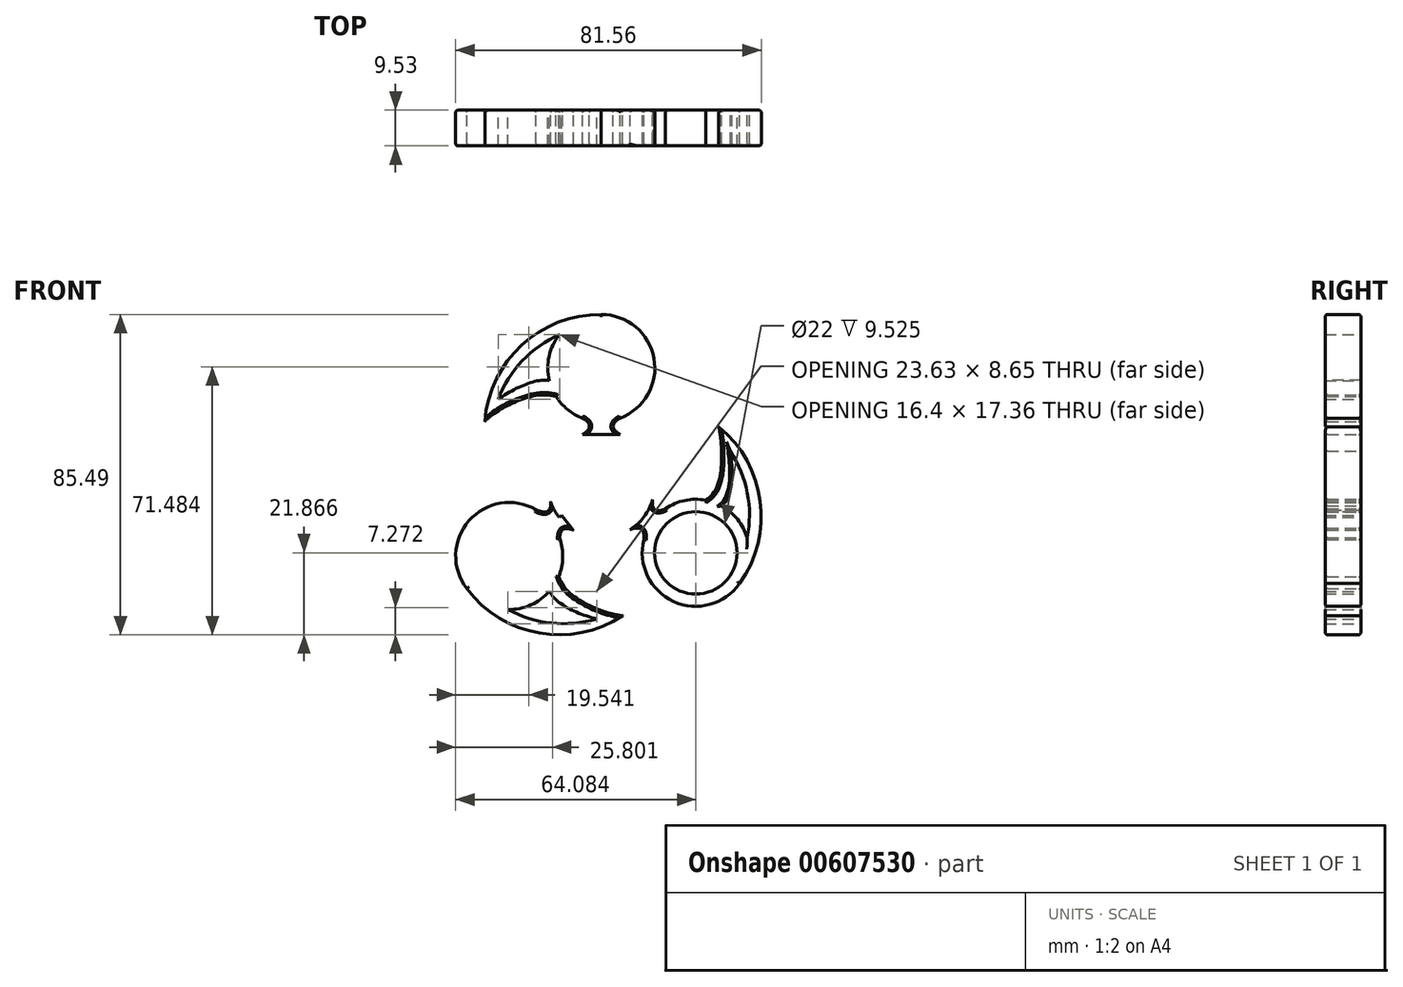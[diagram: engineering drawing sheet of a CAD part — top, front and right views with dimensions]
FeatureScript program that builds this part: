
annotation { "Feature Type Name" : "Feature", "Feature Type Description" : "" }
export const myFeature = defineFeature(function(context is Context, id is Id, definition is map)
    precondition{}
    {
        {
            var Q0;
            Q0=qCreatedBy(makeId("Front.planeOp"),FACE);
            var sketch = newSketch(context, id + "F0", { "sketchPlane" : qUnion([Q0])});
            skCircle(sketch, "E0", {"center": v(0, 0) * mm, "radius": 14.29 * mm});
            skLineSegment(sketch, "E1", {"start": v(0, 0) * mm, "end": v(0, 14.29) * mm});
            skLineSegment(sketch, "E2", {"start": v(0, 0) * mm, "end": v(-11.3, -8.76) * mm});
            skLineSegment(sketch, "E3", {"start": v(0, 0) * mm, "end": v(11.43, -8.57) * mm});
            skCircle(sketch, "E4", {"center": v(0, 31.12) * mm, "radius": 14.29 * mm});
            skLineSegment(sketch, "E5", {"start": v(0, 14.29) * mm, "end": v(0, 16.83) * mm});
            skArc(sketch, "E6", {"start": v(0, 45.4) * mm, "mid": v(-21.2, 37.27) * mm, "end": v(-31.1, 16.83) * mm});
            skFitSpline(sketch, "E7", {"points": [v(-31.1, 16.83) * mm, v(-17.35, 23.79) * mm, v(0, 16.83) * mm], "startDerivative": vector(18.3, 19.68) * mm, "endDerivative": vector(52.34, -33.11) * mm});
            skLineSegment(sketch, "E8", {"start": v(0, 15.56) * mm, "end": v(-3.18, 15.56) * mm});
            skPoint(sketch, "E8.endSnap0", {"position": v(0, 15.56) * mm});
            skLineSegment(sketch, "E9", {"start": v(0, 15.56) * mm, "end": v(3.18, 15.56) * mm});
            skLineSegment(sketch, "E10", {"start": v(0, 17.74) * mm, "end": v(5.03, 17.74) * mm});
            skLineSegment(sketch, "E11", {"start": v(0, 17.74) * mm, "end": v(-5.03, 17.74) * mm});
            skLineSegment(sketch, "E12", {"start": v(0, 14.29) * mm, "end": v(0, 13.37) * mm});
            skLineSegment(sketch, "E13", {"start": v(0, 13.37) * mm, "end": v(-5.03, 13.37) * mm});
            skLineSegment(sketch, "E14", {"start": v(0, 13.37) * mm, "end": v(5.03, 13.37) * mm});
            skFitSpline(sketch, "E15", {"points": [v(-5.03, 17.74) * mm, v(-3.18, 15.56) * mm, v(-5.03, 13.37) * mm], "startDerivative": vector(7.47, -4.37) * mm, "endDerivative": vector(-7.47, -4.37) * mm});
            skFitSpline(sketch, "E16", {"points": [v(5.03, 13.37) * mm, v(3.18, 15.56) * mm, v(5.03, 17.74) * mm], "startDerivative": vector(-7.47, 4.37) * mm, "endDerivative": vector(7.47, 4.37) * mm});
            skArc(sketch, "E17", {"start": v(4.36, 42.56) * mm, "mid": v(-16.61, 36.94) * mm, "end": v(-28.69, 18.9) * mm});
            skFitSpline(sketch, "E18", {"points": [v(-30.7, 19.98) * mm, v(-16.8, 27.72) * mm, v(0.44, 19.97) * mm], "startDerivative": vector(18.3, 19.68) * mm, "endDerivative": vector(52.34, -33.11) * mm});
            skLineSegment(sketch, "E19", {"start": v(-3.18, 15.56) * mm, "end": v(0, 14.29) * mm});
            skLineSegment(sketch, "E20", {"start": v(0, 14.29) * mm, "end": v(3.18, 15.56) * mm});
            skCircle(sketch, "E21", {"center": v(25.21, -18.22) * mm, "radius": 14.29 * mm});
            skLineSegment(sketch, "E22", {"start": v(11.43, -8.57) * mm, "end": v(13.51, -10.03) * mm});
            skArc(sketch, "E23", {"start": v(36.92, -26.42) * mm, "mid": v(42.42, -4.39) * mm, "end": v(31.34, 15.44) * mm});
            skFitSpline(sketch, "E24", {"points": [v(31.34, 15.44) * mm, v(30.71, -0.93) * mm, v(13.51, -10.03) * mm], "startDerivative": vector(5.62, -26.28) * mm, "endDerivative": vector(-57.15, -23.88) * mm});
            skLineSegment(sketch, "E25", {"start": v(12.47, -9.3) * mm, "end": v(14.3, -6.7) * mm});
            skPoint(sketch, "E25.endSnap0", {"position": v(12.47, -9.3) * mm});
            skLineSegment(sketch, "E26", {"start": v(12.47, -9.3) * mm, "end": v(10.65, -11.9) * mm});
            skLineSegment(sketch, "E27", {"start": v(14.26, -10.55) * mm, "end": v(11.38, -14.67) * mm});
            skLineSegment(sketch, "E28", {"start": v(14.26, -10.55) * mm, "end": v(17.14, -6.43) * mm});
            skArc(sketch, "E29", {"start": v(32.04, -28.23) * mm, "mid": v(39.54, -7.93) * mm, "end": v(31.84, 12.3) * mm});
            skFitSpline(sketch, "E30", {"points": [v(33.7, 13.3) * mm, v(33.83, -3.4) * mm, v(15.84, -12.2) * mm], "startDerivative": vector(5.62, -26.28) * mm, "endDerivative": vector(-57.15, -23.88) * mm});
            skLineSegment(sketch, "E31", {"start": v(14.3, -6.7) * mm, "end": v(11.8, -8.05) * mm});
            skLineSegment(sketch, "E32", {"start": v(11.43, -8.57) * mm, "end": v(10.65, -11.9) * mm});
            skLineSegment(sketch, "E33.0", {"start": v(14.3, -6.7) * mm, "end": v(12.47, -9.3) * mm, "construction": true});
            skCircle(sketch, "E34", {"center": v(-24.58, -19.07) * mm, "radius": 14.29 * mm});
            skLineSegment(sketch, "E35", {"start": v(-11.3, -8.76) * mm, "end": v(-13.26, -10.36) * mm});
            skArc(sketch, "E36", {"start": v(-35.91, -27.78) * mm, "mid": v(-16.54, -39.63) * mm, "end": v(5.7, -35.02) * mm});
            skFitSpline(sketch, "E37", {"points": [v(5.7, -35.02) * mm, v(-8.63, -28.76) * mm, v(-13.26, -10.36) * mm], "startDerivative": vector(-26.76, 2.52) * mm, "endDerivative": vector(-5.64, 61.68) * mm});
            skLineSegment(sketch, "E38", {"start": v(-12.27, -9.56) * mm, "end": v(-10.26, -12.02) * mm});
            skPoint(sketch, "E38.endSnap0", {"position": v(-12.27, -9.56) * mm});
            skLineSegment(sketch, "E39", {"start": v(-12.27, -9.56) * mm, "end": v(-14.28, -7.1) * mm});
            skLineSegment(sketch, "E40", {"start": v(-13.97, -10.94) * mm, "end": v(-17.43, -6.7) * mm});
            skLineSegment(sketch, "E41", {"start": v(-13.97, -10.94) * mm, "end": v(-11.04, -14.51) * mm});
            skArc(sketch, "E42", {"start": v(-36.27, -22.58) * mm, "mid": v(-19.07, -35.8) * mm, "end": v(2.57, -34.43) * mm});
            skFitSpline(sketch, "E43", {"points": [v(2.95, -36.62) * mm, v(-12.05, -30.77) * mm, v(-16.16, -11.65) * mm], "startDerivative": vector(-26.76, 2.52) * mm, "endDerivative": vector(-5.64, 61.68) * mm});
            skLineSegment(sketch, "E44", {"start": v(-10.26, -12.02) * mm, "end": v(-10.8, -9.23) * mm});
            skLineSegment(sketch, "E45", {"start": v(-11.3, -8.76) * mm, "end": v(-14.28, -7.1) * mm});
            skLineSegment(sketch, "E46.0", {"start": v(-10.26, -12.02) * mm, "end": v(-12.27, -9.56) * mm, "construction": true});
            skLineSegment(sketch, "E47", {"start": v(-11.3, -8.76) * mm, "end": v(-10.57, -8.2) * mm});
            skLineSegment(sketch, "E48", {"start": v(11.43, -8.57) * mm, "end": v(10.7, -8.02) * mm});
            skLineSegment(sketch, "E49", {"start": v(10.7, -8.02) * mm, "end": v(13.72, -4) * mm});
            skLineSegment(sketch, "E50", {"start": v(10.7, -8.02) * mm, "end": v(7.68, -12.05) * mm});
            skLineSegment(sketch, "E51", {"start": v(-10.57, -8.2) * mm, "end": v(-13.54, -4.56) * mm});
            skLineSegment(sketch, "E52", {"start": v(-10.57, -8.2) * mm, "end": v(-7.49, -12.17) * mm});
            skFitSpline(sketch, "E53", {"points": [v(-13.54, -4.56) * mm, v(-14.28, -7.1) * mm, v(-17.43, -6.7) * mm], "startDerivative": vector(0.73, -8.28) * mm, "endDerivative": vector(-8.38, 3.81) * mm});
            skFitSpline(sketch, "E54", {"points": [v(-11.04, -14.51) * mm, v(-10.26, -12.02) * mm, v(-7.49, -12.17) * mm], "startDerivative": vector(-0.57, 7.9) * mm, "endDerivative": vector(7.64, -3.14) * mm});
            skFitSpline(sketch, "E55", {"points": [v(7.68, -12.05) * mm, v(10.65, -11.9) * mm, v(11.38, -14.67) * mm], "startDerivative": vector(8.1, 3.32) * mm, "endDerivative": vector(-0.74, -8.6) * mm});
            skFitSpline(sketch, "E56", {"points": [v(13.72, -4) * mm, v(14.3, -6.7) * mm, v(17.14, -6.43) * mm], "startDerivative": vector(-1.06, -8.48) * mm, "endDerivative": vector(7.9, 3.59) * mm});
            skSolve(sketch);
        }
        {
            var Q0;
            {var subQ0=sQuery(id+"F0.wireOp",EDGE,"E6");var subQ1=sQuery(id+"F0.wireOp",EDGE,"E4");var subQ2=makeQuery(id+"F0.imprint","INTERSECT",VERTEX,{"derivedFrom":[subQ1,subQ0]});Q0=makeQuery(id+"F0.imprint","IMPRINT",FACE,{"disambiguationData":[TD([[makeQuery(id+"F0.imprint","IMPRINT",EDGE,{"disambiguationData":[TD([[subQ2,-1.0]])],"derivedFrom":subQ1}),-1.0]])]});}
            var Q1;
            {var subQ0=sQuery(id+"F0.wireOp",EDGE,"E18");var subQ1=sQuery(id+"F0.wireOp",EDGE,"E4");var subQ2=makeQuery(id+"F0.imprint","INTERSECT",VERTEX,{"derivedFrom":[subQ1,subQ0]});Q1=makeQuery(id+"F0.imprint","IMPRINT",FACE,{"disambiguationData":[TD([[makeQuery(id+"F0.imprint","IMPRINT",EDGE,{"disambiguationData":[TD([[subQ2,-1.0]])],"derivedFrom":subQ1}),-1.0]])]});}
            var Q2;
            {var subQ0=sQuery(id+"F0.wireOp",EDGE,"E7");var subQ1=sQuery(id+"F0.wireOp",EDGE,"E6");var subQ2=makeQuery(id+"F0.imprint","INTERSECT",VERTEX,{"derivedFrom":[subQ1,subQ0]});Q2=makeQuery(id+"F0.imprint","IMPRINT",FACE,{"disambiguationData":[TD([[makeQuery(id+"F0.imprint","IMPRINT",EDGE,{"disambiguationData":[TD([[subQ2,1.0]])],"derivedFrom":subQ1}),1.0]])]});}
            var Q3;
            {var subQ7=sQuery(id+"F0.wireOp",EDGE,"E10");Q3=makeQuery(id+"F0.imprint","IMPRINT",FACE,{"disambiguationData":[TD([[makeQuery(id+"F0.imprint","IMPRINT",EDGE,{"derivedFrom":subQ7}),1.0]])]});}
            var Q4;
            Q4=makeQuery(id+"F0.imprint","IMPRINT",FACE,{"disambiguationData":[TD([[makeQuery(id+"F0.imprint","IMPRINT",EDGE,{"derivedFrom":sQuery(id+"F0.wireOp",EDGE,"E1")}),1.0]])]});
            var Q5;
            Q5=makeQuery(id+"F0.imprint","IMPRINT",FACE,{"disambiguationData":[TD([[makeQuery(id+"F0.imprint","IMPRINT",EDGE,{"derivedFrom":sQuery(id+"F0.wireOp",EDGE,"E2")}),1.0]])]});
            var Q6;
            Q6=makeQuery(id+"F0.imprint","IMPRINT",FACE,{"disambiguationData":[TD([[makeQuery(id+"F0.imprint","IMPRINT",EDGE,{"derivedFrom":sQuery(id+"F0.wireOp",EDGE,"E1")}),-1.0]])]});
            var Q7;
            {var subQ7=sQuery(id+"F0.wireOp",EDGE,"E40");Q7=makeQuery(id+"F0.imprint","IMPRINT",FACE,{"disambiguationData":[TD([[makeQuery(id+"F0.imprint","IMPRINT",EDGE,{"derivedFrom":subQ7}),1.0]])]});}
            var Q8;
            {var subQ0=sQuery(id+"F0.wireOp",EDGE,"E36");var subQ1=sQuery(id+"F0.wireOp",EDGE,"E34");var subQ2=makeQuery(id+"F0.imprint","INTERSECT",VERTEX,{"derivedFrom":[subQ1,subQ0]});Q8=makeQuery(id+"F0.imprint","IMPRINT",FACE,{"disambiguationData":[TD([[makeQuery(id+"F0.imprint","IMPRINT",EDGE,{"disambiguationData":[TD([[subQ2,-1.0]])],"derivedFrom":subQ1}),-1.0]])]});}
            var Q9;
            {var subQ0=sQuery(id+"F0.wireOp",EDGE,"E43");var subQ1=sQuery(id+"F0.wireOp",EDGE,"E34");var subQ2=makeQuery(id+"F0.imprint","INTERSECT",VERTEX,{"derivedFrom":[subQ1,subQ0]});Q9=makeQuery(id+"F0.imprint","IMPRINT",FACE,{"disambiguationData":[TD([[makeQuery(id+"F0.imprint","IMPRINT",EDGE,{"disambiguationData":[TD([[subQ2,-1.0]])],"derivedFrom":subQ1}),-1.0]])]});}
            var Q10;
            {var subQ0=sQuery(id+"F0.wireOp",EDGE,"E37");var subQ1=sQuery(id+"F0.wireOp",EDGE,"E36");var subQ2=makeQuery(id+"F0.imprint","INTERSECT",VERTEX,{"derivedFrom":[subQ1,subQ0]});Q10=makeQuery(id+"F0.imprint","IMPRINT",FACE,{"disambiguationData":[TD([[makeQuery(id+"F0.imprint","IMPRINT",EDGE,{"disambiguationData":[TD([[subQ2,1.0]])],"derivedFrom":subQ1}),1.0]])]});}
            var Q11;
            {var subQ1=sQuery(id+"F0.wireOp",EDGE,"E34");var subQ3=sQuery(id+"F0.wireOp",EDGE,"E37");var subQ4=makeQuery(id+"F0.imprint","INTERSECT",VERTEX,{"derivedFrom":[subQ1,subQ3]});Q11=makeQuery(id+"F0.imprint","IMPRINT",FACE,{"disambiguationData":[TD([[makeQuery(id+"F0.imprint","IMPRINT",EDGE,{"disambiguationData":[TD([[subQ4,-1.0]])],"derivedFrom":subQ3}),-1.0]])]});}
            var Q12;
            {var subQ5=sQuery(id+"F0.wireOp",EDGE,"E27");Q12=makeQuery(id+"F0.imprint","IMPRINT",FACE,{"disambiguationData":[TD([[makeQuery(id+"F0.imprint","IMPRINT",EDGE,{"derivedFrom":subQ5}),1.0]])]});}
            var Q13;
            {var subQ0=sQuery(id+"F0.wireOp",EDGE,"E23");var subQ1=sQuery(id+"F0.wireOp",EDGE,"E21");var subQ2=makeQuery(id+"F0.imprint","INTERSECT",VERTEX,{"derivedFrom":[subQ1,subQ0]});Q13=makeQuery(id+"F0.imprint","IMPRINT",FACE,{"disambiguationData":[TD([[makeQuery(id+"F0.imprint","IMPRINT",EDGE,{"disambiguationData":[TD([[subQ2,-1.0]])],"derivedFrom":subQ1}),-1.0]])]});}
            var Q14;
            {var subQ0=sQuery(id+"F0.wireOp",EDGE,"E30");var subQ1=sQuery(id+"F0.wireOp",EDGE,"E21");var subQ2=makeQuery(id+"F0.imprint","INTERSECT",VERTEX,{"derivedFrom":[subQ1,subQ0]});Q14=makeQuery(id+"F0.imprint","IMPRINT",FACE,{"disambiguationData":[TD([[makeQuery(id+"F0.imprint","IMPRINT",EDGE,{"disambiguationData":[TD([[subQ2,-1.0]])],"derivedFrom":subQ1}),-1.0]])]});}
            var Q15;
            {var subQ0=sQuery(id+"F0.wireOp",EDGE,"E24");var subQ1=sQuery(id+"F0.wireOp",EDGE,"E23");var subQ2=makeQuery(id+"F0.imprint","INTERSECT",VERTEX,{"derivedFrom":[subQ1,subQ0]});Q15=makeQuery(id+"F0.imprint","IMPRINT",FACE,{"disambiguationData":[TD([[makeQuery(id+"F0.imprint","IMPRINT",EDGE,{"disambiguationData":[TD([[subQ2,1.0]])],"derivedFrom":subQ1}),1.0]])]});}
            var Q16;
            {var subQ0=sQuery(id+"F0.wireOp",EDGE,"E28");var subQ1=sQuery(id+"F0.wireOp",EDGE,"E21");var subQ2=makeQuery(id+"F0.imprint","INTERSECT",VERTEX,{"derivedFrom":[subQ1,subQ0]});Q16=makeQuery(id+"F0.imprint","IMPRINT",FACE,{"disambiguationData":[TD([[makeQuery(id+"F0.imprint","IMPRINT",EDGE,{"disambiguationData":[TD([[subQ2,1.0]])],"derivedFrom":subQ1}),1.0]])]});}
            var Q17;
            {var subQ3=sQuery(id+"F0.wireOp",EDGE,"E40");Q17=makeQuery(id+"F0.imprint","IMPRINT",FACE,{"disambiguationData":[TD([[makeQuery(id+"F0.imprint","IMPRINT",EDGE,{"derivedFrom":subQ3}),-1.0]])]});}
            var Q18;
            {var subQ0=sQuery(id+"F0.wireOp",EDGE,"E37");var subQ3=sQuery(id+"F0.wireOp",EDGE,"E41");var subQ5=makeQuery(id+"F0.imprint","INTERSECT",VERTEX,{"derivedFrom":[subQ0,subQ3]});Q18=makeQuery(id+"F0.imprint","IMPRINT",FACE,{"disambiguationData":[TD([[makeQuery(id+"F0.imprint","IMPRINT",EDGE,{"disambiguationData":[TD([[subQ5,-1.0]])],"derivedFrom":subQ0}),-1.0]])]});}
            var Q19;
            {var subQ0=sQuery(id+"F0.wireOp",EDGE,"E47");Q19=makeQuery(id+"F0.imprint","IMPRINT",FACE,{"disambiguationData":[TD([[makeQuery(id+"F0.imprint","IMPRINT",EDGE,{"derivedFrom":subQ0}),-1.0]])]});}
            var Q20;
            {var subQ0=sQuery(id+"F0.wireOp",EDGE,"E47");Q20=makeQuery(id+"F0.imprint","IMPRINT",FACE,{"disambiguationData":[TD([[makeQuery(id+"F0.imprint","IMPRINT",EDGE,{"derivedFrom":subQ0}),1.0]])]});}
            var Q21;
            {var subQ0=sQuery(id+"F0.wireOp",EDGE,"E45");Q21=makeQuery(id+"F0.imprint","IMPRINT",FACE,{"disambiguationData":[TD([[makeQuery(id+"F0.imprint","IMPRINT",EDGE,{"derivedFrom":subQ0}),-1.0]])]});}
            var Q22;
            {var subQ1=sQuery(id+"F0.wireOp",EDGE,"E0");var subQ3=sQuery(id+"F0.wireOp",EDGE,"E44");var subQ4=makeQuery(id+"F0.imprint","INTERSECT",VERTEX,{"derivedFrom":[subQ1,subQ3]});Q22=makeQuery(id+"F0.imprint","IMPRINT",FACE,{"disambiguationData":[TD([[makeQuery(id+"F0.imprint","IMPRINT",EDGE,{"disambiguationData":[TD([[subQ4,-1.0]])],"derivedFrom":subQ1}),-1.0]])]});}
            var Q23;
            {var subQ5=sQuery(id+"F0.wireOp",EDGE,"E38");Q23=makeQuery(id+"F0.imprint","IMPRINT",FACE,{"disambiguationData":[TD([[makeQuery(id+"F0.imprint","IMPRINT",EDGE,{"derivedFrom":subQ5}),-1.0]])]});}
            var Q24;
            {var subQ5=sQuery(id+"F0.wireOp",EDGE,"E39");Q24=makeQuery(id+"F0.imprint","IMPRINT",FACE,{"disambiguationData":[TD([[makeQuery(id+"F0.imprint","IMPRINT",EDGE,{"derivedFrom":subQ5}),1.0]])]});}
            var Q25;
            {var subQ2=sQuery(id+"F0.wireOp",EDGE,"E39");Q25=makeQuery(id+"F0.imprint","IMPRINT",FACE,{"disambiguationData":[TD([[makeQuery(id+"F0.imprint","IMPRINT",EDGE,{"derivedFrom":subQ2}),-1.0]])]});}
            var Q26;
            {var subQ5=sQuery(id+"F0.wireOp",EDGE,"E38");Q26=makeQuery(id+"F0.imprint","IMPRINT",FACE,{"disambiguationData":[TD([[makeQuery(id+"F0.imprint","IMPRINT",EDGE,{"derivedFrom":subQ5}),1.0]])]});}
            var Q27;
            {var subQ3=sQuery(id+"F0.wireOp",EDGE,"E27");Q27=makeQuery(id+"F0.imprint","IMPRINT",FACE,{"disambiguationData":[TD([[makeQuery(id+"F0.imprint","IMPRINT",EDGE,{"derivedFrom":subQ3}),-1.0]])]});}
            var Q28;
            {var subQ0=sQuery(id+"F0.wireOp",EDGE,"E24");var subQ3=sQuery(id+"F0.wireOp",EDGE,"E28");var subQ5=makeQuery(id+"F0.imprint","INTERSECT",VERTEX,{"derivedFrom":[subQ0,subQ3]});Q28=makeQuery(id+"F0.imprint","IMPRINT",FACE,{"disambiguationData":[TD([[makeQuery(id+"F0.imprint","IMPRINT",EDGE,{"disambiguationData":[TD([[subQ5,-1.0]])],"derivedFrom":subQ0}),-1.0]])]});}
            var Q29;
            {var subQ5=sQuery(id+"F0.wireOp",EDGE,"E25");Q29=makeQuery(id+"F0.imprint","IMPRINT",FACE,{"disambiguationData":[TD([[makeQuery(id+"F0.imprint","IMPRINT",EDGE,{"derivedFrom":subQ5}),-1.0]])]});}
            var Q30;
            {var subQ2=sQuery(id+"F0.wireOp",EDGE,"E25");Q30=makeQuery(id+"F0.imprint","IMPRINT",FACE,{"disambiguationData":[TD([[makeQuery(id+"F0.imprint","IMPRINT",EDGE,{"derivedFrom":subQ2}),1.0]])]});}
            var Q31;
            {var subQ0=sQuery(id+"F0.wireOp",EDGE,"E31");Q31=makeQuery(id+"F0.imprint","IMPRINT",FACE,{"disambiguationData":[TD([[makeQuery(id+"F0.imprint","IMPRINT",EDGE,{"derivedFrom":subQ0}),-1.0]])]});}
            var Q32;
            {var subQ0=sQuery(id+"F0.wireOp",EDGE,"E48");Q32=makeQuery(id+"F0.imprint","IMPRINT",FACE,{"disambiguationData":[TD([[makeQuery(id+"F0.imprint","IMPRINT",EDGE,{"derivedFrom":subQ0}),-1.0]])]});}
            var Q33;
            {var subQ0=sQuery(id+"F0.wireOp",EDGE,"E48");Q33=makeQuery(id+"F0.imprint","IMPRINT",FACE,{"disambiguationData":[TD([[makeQuery(id+"F0.imprint","IMPRINT",EDGE,{"derivedFrom":subQ0}),1.0]])]});}
            var Q34;
            {var subQ0=sQuery(id+"F0.wireOp",EDGE,"E32");Q34=makeQuery(id+"F0.imprint","IMPRINT",FACE,{"disambiguationData":[TD([[makeQuery(id+"F0.imprint","IMPRINT",EDGE,{"derivedFrom":subQ0}),-1.0]])]});}
            var Q35;
            {var subQ2=sQuery(id+"F0.wireOp",EDGE,"E26");Q35=makeQuery(id+"F0.imprint","IMPRINT",FACE,{"disambiguationData":[TD([[makeQuery(id+"F0.imprint","IMPRINT",EDGE,{"derivedFrom":subQ2}),-1.0]])]});}
            var Q36;
            {var subQ5=sQuery(id+"F0.wireOp",EDGE,"E26");Q36=makeQuery(id+"F0.imprint","IMPRINT",FACE,{"disambiguationData":[TD([[makeQuery(id+"F0.imprint","IMPRINT",EDGE,{"derivedFrom":subQ5}),1.0]])]});}
            var Q37;
            {var subQ1=sQuery(id+"F0.wireOp",EDGE,"E4");var subQ3=sQuery(id+"F0.wireOp",EDGE,"E7");var subQ4=makeQuery(id+"F0.imprint","INTERSECT",VERTEX,{"derivedFrom":[subQ1,subQ3]});Q37=makeQuery(id+"F0.imprint","IMPRINT",FACE,{"disambiguationData":[TD([[makeQuery(id+"F0.imprint","IMPRINT",EDGE,{"disambiguationData":[TD([[subQ4,-1.0]])],"derivedFrom":subQ3}),-1.0]])]});}
            var Q38;
            {var subQ0=sQuery(id+"F0.wireOp",EDGE,"E7");var subQ3=sQuery(id+"F0.wireOp",EDGE,"E11");var subQ5=makeQuery(id+"F0.imprint","INTERSECT",VERTEX,{"derivedFrom":[subQ0,subQ3]});Q38=makeQuery(id+"F0.imprint","IMPRINT",FACE,{"disambiguationData":[TD([[makeQuery(id+"F0.imprint","IMPRINT",EDGE,{"disambiguationData":[TD([[subQ5,-1.0]])],"derivedFrom":subQ0}),-1.0]])]});}
            var Q39;
            {var subQ5=sQuery(id+"F0.wireOp",EDGE,"E8");Q39=makeQuery(id+"F0.imprint","IMPRINT",FACE,{"disambiguationData":[TD([[makeQuery(id+"F0.imprint","IMPRINT",EDGE,{"derivedFrom":subQ5}),-1.0]])]});}
            var Q40;
            {var subQ0=sQuery(id+"F0.wireOp",EDGE,"E20");Q40=makeQuery(id+"F0.imprint","IMPRINT",FACE,{"disambiguationData":[TD([[makeQuery(id+"F0.imprint","IMPRINT",EDGE,{"derivedFrom":subQ0}),-1.0]])]});}
            var Q41;
            {var subQ0=sQuery(id+"F0.wireOp",EDGE,"E12");Q41=makeQuery(id+"F0.imprint","IMPRINT",FACE,{"disambiguationData":[TD([[makeQuery(id+"F0.imprint","IMPRINT",EDGE,{"derivedFrom":subQ0}),1.0]])]});}
            var Q42;
            {var subQ0=sQuery(id+"F0.wireOp",EDGE,"E12");Q42=makeQuery(id+"F0.imprint","IMPRINT",FACE,{"disambiguationData":[TD([[makeQuery(id+"F0.imprint","IMPRINT",EDGE,{"derivedFrom":subQ0}),-1.0]])]});}
            var Q43;
            {var subQ0=sQuery(id+"F0.wireOp",EDGE,"E19");Q43=makeQuery(id+"F0.imprint","IMPRINT",FACE,{"disambiguationData":[TD([[makeQuery(id+"F0.imprint","IMPRINT",EDGE,{"derivedFrom":subQ0}),-1.0]])]});}
            var Q44;
            {var subQ2=sQuery(id+"F0.wireOp",EDGE,"E8");Q44=makeQuery(id+"F0.imprint","IMPRINT",FACE,{"disambiguationData":[TD([[makeQuery(id+"F0.imprint","IMPRINT",EDGE,{"derivedFrom":subQ2}),1.0]])]});}
            var Q45;
            {var subQ2=sQuery(id+"F0.wireOp",EDGE,"E9");Q45=makeQuery(id+"F0.imprint","IMPRINT",FACE,{"disambiguationData":[TD([[makeQuery(id+"F0.imprint","IMPRINT",EDGE,{"derivedFrom":subQ2}),-1.0]])]});}
            var Q46;
            {var subQ5=sQuery(id+"F0.wireOp",EDGE,"E9");Q46=makeQuery(id+"F0.imprint","IMPRINT",FACE,{"disambiguationData":[TD([[makeQuery(id+"F0.imprint","IMPRINT",EDGE,{"derivedFrom":subQ5}),1.0]])]});}
            var Q47;
            {var subQ3=sQuery(id+"F0.wireOp",EDGE,"E10");Q47=makeQuery(id+"F0.imprint","IMPRINT",FACE,{"disambiguationData":[TD([[makeQuery(id+"F0.imprint","IMPRINT",EDGE,{"derivedFrom":subQ3}),-1.0]])]});}
            extrude(context, id + "F1", {"entities" : qUnion([Q0, Q1, Q2, Q3, Q4, Q5, Q6, Q7, Q8, Q9, Q10, Q11, Q12, Q13, Q14, Q15, Q16, Q17, Q18, Q19, Q20, Q21, Q22, Q23, Q24, Q25, Q26, Q27, Q28, Q29, Q30, Q31, Q32, Q33, Q34, Q35, Q36, Q37, Q38, Q39, Q40, Q41, Q42, Q43, Q44, Q45, Q46, Q47]), "depth" : 9.52 * mm, "offsetDistance" : 25.4 * mm});
        }
        {
            var Q0;
            {var subQ0=sQuery(id+"F0.wireOp",EDGE,"E4");Q0=makeQuery(id+"F1.opExtrude","CAP_EDGE",EDGE,{"disambiguationData":[OSD([subQ0]),TDD([makeQuery(id+"F0.imprint","IMPRINT",EDGE,{"disambiguationData":[TD([[makeQuery(id+"F0.imprint","INTERSECT",VERTEX,{"derivedFrom":[subQ0,sQuery(id+"F0.wireOp",EDGE,"E7")]}),-1.0]])],"derivedFrom":subQ0})])],"isStart":false});}
            var Q1;
            Q1=makeQuery(id+"F1.opExtrude","CAP_EDGE",EDGE,{"disambiguationData":[OSD([sQuery(id+"F0.wireOp",EDGE,"E15")])],"isStart":false});
            var Q2;
            {var subQ0=sQuery(id+"F0.wireOp",EDGE,"E0");Q2=makeQuery(id+"F1.opExtrude","CAP_EDGE",EDGE,{"disambiguationData":[OSD([subQ0]),TDD([makeQuery(id+"F0.imprint","IMPRINT",EDGE,{"disambiguationData":[TD([[makeQuery(id+"F0.imprint","INTERSECT",VERTEX,{"derivedFrom":[subQ0,sQuery(id+"F0.wireOp",EDGE,"E13"),sQuery(id+"F0.wireOp",EDGE,"E15")]}),-1.0]])],"derivedFrom":subQ0})])],"isStart":false});}
            var Q3;
            Q3=makeQuery(id+"F1.opExtrude","CAP_EDGE",EDGE,{"disambiguationData":[OSD([sQuery(id+"F0.wireOp",EDGE,"E53")])],"isStart":false});
            var Q4;
            {var subQ0=sQuery(id+"F0.wireOp",EDGE,"E34");Q4=makeQuery(id+"F1.opExtrude","CAP_EDGE",EDGE,{"disambiguationData":[OSD([subQ0]),TDD([makeQuery(id+"F0.imprint","IMPRINT",EDGE,{"disambiguationData":[TD([[makeQuery(id+"F0.imprint","INTERSECT",VERTEX,{"derivedFrom":[subQ0,sQuery(id+"F0.wireOp",EDGE,"E36")]}),1.0]])],"derivedFrom":subQ0})])],"isStart":false});}
            var Q5;
            Q5=makeQuery(id+"F1.opExtrude","CAP_EDGE",EDGE,{"disambiguationData":[OSD([sQuery(id+"F0.wireOp",EDGE,"E36")])],"isStart":false});
            var Q6;
            Q6=makeQuery(id+"F1.opExtrude","CAP_EDGE",EDGE,{"disambiguationData":[OSD([sQuery(id+"F0.wireOp",EDGE,"E37")])],"isStart":false});
            var Q7;
            Q7=makeQuery(id+"F1.opExtrude","CAP_FACE",FACE,{"disambiguationData":[OSD([sQuery(id+"F0.wireOp",EDGE,"E0"),sQuery(id+"F0.wireOp",EDGE,"E4"),sQuery(id+"F0.wireOp",EDGE,"E6"),sQuery(id+"F0.wireOp",EDGE,"E7"),sQuery(id+"F0.wireOp",EDGE,"E15"),sQuery(id+"F0.wireOp",EDGE,"E16"),sQuery(id+"F0.wireOp",EDGE,"E17"),sQuery(id+"F0.wireOp",EDGE,"E18"),sQuery(id+"F0.wireOp",EDGE,"E21"),sQuery(id+"F0.wireOp",EDGE,"E23"),sQuery(id+"F0.wireOp",EDGE,"E24"),sQuery(id+"F0.wireOp",EDGE,"E29"),sQuery(id+"F0.wireOp",EDGE,"E30"),sQuery(id+"F0.wireOp",EDGE,"E34"),sQuery(id+"F0.wireOp",EDGE,"E36"),sQuery(id+"F0.wireOp",EDGE,"E37"),sQuery(id+"F0.wireOp",EDGE,"E42"),sQuery(id+"F0.wireOp",EDGE,"E43"),sQuery(id+"F0.wireOp",EDGE,"E53"),sQuery(id+"F0.wireOp",EDGE,"E54"),sQuery(id+"F0.wireOp",EDGE,"E55"),sQuery(id+"F0.wireOp",EDGE,"E56")])],"isStart":false});
            var Q8;
            Q8=makeQuery(id+"F1.opExtrude","CAP_EDGE",EDGE,{"disambiguationData":[OSD([sQuery(id+"F0.wireOp",EDGE,"E7")])],"isStart":false});
            var Q9;
            Q9=makeQuery(id+"F1.opExtrude","CAP_EDGE",EDGE,{"disambiguationData":[OSD([sQuery(id+"F0.wireOp",EDGE,"E54")])],"isStart":false});
            var Q10;
            {var subQ0=sQuery(id+"F0.wireOp",EDGE,"E34");Q10=makeQuery(id+"F1.opExtrude","CAP_EDGE",EDGE,{"disambiguationData":[OSD([subQ0]),TDD([makeQuery(id+"F0.imprint","IMPRINT",EDGE,{"disambiguationData":[TD([[makeQuery(id+"F0.imprint","INTERSECT",VERTEX,{"derivedFrom":[subQ0,sQuery(id+"F0.wireOp",EDGE,"E37")]}),-1.0]])],"derivedFrom":subQ0})])],"isStart":false});}
            var Q11;
            {var subQ0=sQuery(id+"F0.wireOp",EDGE,"E0");Q11=makeQuery(id+"F1.opExtrude","CAP_EDGE",EDGE,{"disambiguationData":[OSD([subQ0]),TDD([makeQuery(id+"F0.imprint","IMPRINT",EDGE,{"disambiguationData":[TD([[makeQuery(id+"F0.imprint","INTERSECT",VERTEX,{"derivedFrom":[subQ0,sQuery(id+"F0.wireOp",EDGE,"E50"),sQuery(id+"F0.wireOp",EDGE,"E55")]}),1.0]])],"derivedFrom":subQ0})])],"isStart":false});}
            var Q12;
            Q12=makeQuery(id+"F1.opExtrude","CAP_EDGE",EDGE,{"disambiguationData":[OSD([sQuery(id+"F0.wireOp",EDGE,"E55")])],"isStart":false});
            var Q13;
            {var subQ0=sQuery(id+"F0.wireOp",EDGE,"E21");Q13=makeQuery(id+"F1.opExtrude","CAP_EDGE",EDGE,{"disambiguationData":[OSD([subQ0]),TDD([makeQuery(id+"F0.imprint","IMPRINT",EDGE,{"disambiguationData":[TD([[makeQuery(id+"F0.imprint","INTERSECT",VERTEX,{"derivedFrom":[subQ0,sQuery(id+"F0.wireOp",EDGE,"E23")]}),1.0]])],"derivedFrom":subQ0})])],"isStart":false});}
            var Q14;
            Q14=makeQuery(id+"F1.opExtrude","CAP_EDGE",EDGE,{"disambiguationData":[OSD([sQuery(id+"F0.wireOp",EDGE,"E23")])],"isStart":false});
            var Q15;
            Q15=makeQuery(id+"F1.opExtrude","CAP_EDGE",EDGE,{"disambiguationData":[OSD([sQuery(id+"F0.wireOp",EDGE,"E24")])],"isStart":false});
            var Q16;
            {var subQ0=sQuery(id+"F0.wireOp",EDGE,"E21");Q16=makeQuery(id+"F1.opExtrude","CAP_EDGE",EDGE,{"disambiguationData":[OSD([subQ0]),TDD([makeQuery(id+"F0.imprint","IMPRINT",EDGE,{"disambiguationData":[TD([[makeQuery(id+"F0.imprint","INTERSECT",VERTEX,{"derivedFrom":[subQ0,sQuery(id+"F0.wireOp",EDGE,"E24")]}),-1.0]])],"derivedFrom":subQ0})])],"isStart":false});}
            var Q17;
            Q17=makeQuery(id+"F1.opExtrude","CAP_EDGE",EDGE,{"disambiguationData":[OSD([sQuery(id+"F0.wireOp",EDGE,"E56")])],"isStart":false});
            var Q18;
            {var subQ0=sQuery(id+"F0.wireOp",EDGE,"E0");Q18=makeQuery(id+"F1.opExtrude","CAP_EDGE",EDGE,{"disambiguationData":[OSD([subQ0]),TDD([makeQuery(id+"F0.imprint","IMPRINT",EDGE,{"disambiguationData":[TD([[makeQuery(id+"F0.imprint","INTERSECT",VERTEX,{"derivedFrom":[subQ0,sQuery(id+"F0.wireOp",EDGE,"E14"),sQuery(id+"F0.wireOp",EDGE,"E16")]}),1.0]])],"derivedFrom":subQ0})])],"isStart":false});}
            var Q19;
            Q19=makeQuery(id+"F1.opExtrude","CAP_EDGE",EDGE,{"disambiguationData":[OSD([sQuery(id+"F0.wireOp",EDGE,"E16")])],"isStart":false});
            var Q20;
            {var subQ0=sQuery(id+"F0.wireOp",EDGE,"E4");Q20=makeQuery(id+"F1.opExtrude","CAP_EDGE",EDGE,{"disambiguationData":[OSD([subQ0]),TDD([makeQuery(id+"F0.imprint","IMPRINT",EDGE,{"disambiguationData":[TD([[makeQuery(id+"F0.imprint","INTERSECT",VERTEX,{"derivedFrom":[subQ0,sQuery(id+"F0.wireOp",EDGE,"E6")]}),1.0]])],"derivedFrom":subQ0})])],"isStart":false});}
            var Q21;
            Q21=makeQuery(id+"F1.opExtrude","CAP_EDGE",EDGE,{"disambiguationData":[OSD([sQuery(id+"F0.wireOp",EDGE,"E6")])],"isStart":false});
            var Q22;
            Q22=makeQuery(id+"F1.opExtrude","CAP_EDGE",EDGE,{"disambiguationData":[OSD([sQuery(id+"F0.wireOp",EDGE,"E16")])],"isStart":true});
            var Q23;
            {var subQ0=sQuery(id+"F0.wireOp",EDGE,"E4");Q23=makeQuery(id+"F1.opExtrude","CAP_EDGE",EDGE,{"disambiguationData":[OSD([subQ0]),TDD([makeQuery(id+"F0.imprint","IMPRINT",EDGE,{"disambiguationData":[TD([[makeQuery(id+"F0.imprint","INTERSECT",VERTEX,{"derivedFrom":[subQ0,sQuery(id+"F0.wireOp",EDGE,"E6")]}),1.0]])],"derivedFrom":subQ0})])],"isStart":true});}
            var Q24;
            {var subQ0=sQuery(id+"F0.wireOp",EDGE,"E0");Q24=makeQuery(id+"F1.opExtrude","CAP_EDGE",EDGE,{"disambiguationData":[OSD([subQ0]),TDD([makeQuery(id+"F0.imprint","IMPRINT",EDGE,{"disambiguationData":[TD([[makeQuery(id+"F0.imprint","INTERSECT",VERTEX,{"derivedFrom":[subQ0,sQuery(id+"F0.wireOp",EDGE,"E14"),sQuery(id+"F0.wireOp",EDGE,"E16")]}),1.0]])],"derivedFrom":subQ0})])],"isStart":true});}
            var Q25;
            Q25=makeQuery(id+"F1.opExtrude","CAP_EDGE",EDGE,{"disambiguationData":[OSD([sQuery(id+"F0.wireOp",EDGE,"E56")])],"isStart":true});
            var Q26;
            {var subQ0=sQuery(id+"F0.wireOp",EDGE,"E21");Q26=makeQuery(id+"F1.opExtrude","CAP_EDGE",EDGE,{"disambiguationData":[OSD([subQ0]),TDD([makeQuery(id+"F0.imprint","IMPRINT",EDGE,{"disambiguationData":[TD([[makeQuery(id+"F0.imprint","INTERSECT",VERTEX,{"derivedFrom":[subQ0,sQuery(id+"F0.wireOp",EDGE,"E24")]}),-1.0]])],"derivedFrom":subQ0})])],"isStart":true});}
            var Q27;
            Q27=makeQuery(id+"F1.opExtrude","CAP_EDGE",EDGE,{"disambiguationData":[OSD([sQuery(id+"F0.wireOp",EDGE,"E23")])],"isStart":true});
            var Q28;
            Q28=makeQuery(id+"F1.opExtrude","CAP_EDGE",EDGE,{"disambiguationData":[OSD([sQuery(id+"F0.wireOp",EDGE,"E55")])],"isStart":true});
            var Q29;
            {var subQ0=sQuery(id+"F0.wireOp",EDGE,"E0");Q29=makeQuery(id+"F1.opExtrude","CAP_EDGE",EDGE,{"disambiguationData":[OSD([subQ0]),TDD([makeQuery(id+"F0.imprint","IMPRINT",EDGE,{"disambiguationData":[TD([[makeQuery(id+"F0.imprint","INTERSECT",VERTEX,{"derivedFrom":[subQ0,sQuery(id+"F0.wireOp",EDGE,"E50"),sQuery(id+"F0.wireOp",EDGE,"E55")]}),1.0]])],"derivedFrom":subQ0})])],"isStart":true});}
            var Q30;
            Q30=makeQuery(id+"F1.opExtrude","CAP_EDGE",EDGE,{"disambiguationData":[OSD([sQuery(id+"F0.wireOp",EDGE,"E54")])],"isStart":true});
            var Q31;
            {var subQ0=sQuery(id+"F0.wireOp",EDGE,"E34");Q31=makeQuery(id+"F1.opExtrude","CAP_EDGE",EDGE,{"disambiguationData":[OSD([subQ0]),TDD([makeQuery(id+"F0.imprint","IMPRINT",EDGE,{"disambiguationData":[TD([[makeQuery(id+"F0.imprint","INTERSECT",VERTEX,{"derivedFrom":[subQ0,sQuery(id+"F0.wireOp",EDGE,"E37")]}),-1.0]])],"derivedFrom":subQ0})])],"isStart":true});}
            var Q32;
            Q32=makeQuery(id+"F1.opExtrude","CAP_EDGE",EDGE,{"disambiguationData":[OSD([sQuery(id+"F0.wireOp",EDGE,"E37")])],"isStart":true});
            var Q33;
            Q33=makeQuery(id+"F1.opExtrude","CAP_EDGE",EDGE,{"disambiguationData":[OSD([sQuery(id+"F0.wireOp",EDGE,"E36")])],"isStart":true});
            var Q34;
            Q34=makeQuery(id+"F1.opExtrude","CAP_EDGE",EDGE,{"disambiguationData":[OSD([sQuery(id+"F0.wireOp",EDGE,"E36")])],"isStart":true});
            var Q35;
            {var subQ0=sQuery(id+"F0.wireOp",EDGE,"E34");Q35=makeQuery(id+"F1.opExtrude","CAP_EDGE",EDGE,{"disambiguationData":[OSD([subQ0]),TDD([makeQuery(id+"F0.imprint","IMPRINT",EDGE,{"disambiguationData":[TD([[makeQuery(id+"F0.imprint","INTERSECT",VERTEX,{"derivedFrom":[subQ0,sQuery(id+"F0.wireOp",EDGE,"E36")]}),1.0]])],"derivedFrom":subQ0})])],"isStart":true});}
            var Q36;
            Q36=makeQuery(id+"F1.opExtrude","CAP_EDGE",EDGE,{"disambiguationData":[OSD([sQuery(id+"F0.wireOp",EDGE,"E53")])],"isStart":true});
            var Q37;
            {var subQ0=sQuery(id+"F0.wireOp",EDGE,"E0");Q37=makeQuery(id+"F1.opExtrude","CAP_EDGE",EDGE,{"disambiguationData":[OSD([subQ0]),TDD([makeQuery(id+"F0.imprint","IMPRINT",EDGE,{"disambiguationData":[TD([[makeQuery(id+"F0.imprint","INTERSECT",VERTEX,{"derivedFrom":[subQ0,sQuery(id+"F0.wireOp",EDGE,"E13"),sQuery(id+"F0.wireOp",EDGE,"E15")]}),-1.0]])],"derivedFrom":subQ0})])],"isStart":true});}
            var Q38;
            Q38=makeQuery(id+"F1.opExtrude","CAP_EDGE",EDGE,{"disambiguationData":[OSD([sQuery(id+"F0.wireOp",EDGE,"E15")])],"isStart":true});
            var Q39;
            {var subQ0=sQuery(id+"F0.wireOp",EDGE,"E4");Q39=makeQuery(id+"F1.opExtrude","CAP_EDGE",EDGE,{"disambiguationData":[OSD([subQ0]),TDD([makeQuery(id+"F0.imprint","IMPRINT",EDGE,{"disambiguationData":[TD([[makeQuery(id+"F0.imprint","INTERSECT",VERTEX,{"derivedFrom":[subQ0,sQuery(id+"F0.wireOp",EDGE,"E7")]}),-1.0]])],"derivedFrom":subQ0})])],"isStart":true});}
            var Q40;
            Q40=makeQuery(id+"F1.opExtrude","CAP_EDGE",EDGE,{"disambiguationData":[OSD([sQuery(id+"F0.wireOp",EDGE,"E7")])],"isStart":true});
            var Q41;
            Q41=makeQuery(id+"F1.opExtrude","CAP_EDGE",EDGE,{"disambiguationData":[OSD([sQuery(id+"F0.wireOp",EDGE,"E6")])],"isStart":true});
            var Q42;
            {var subQ0=sQuery(id+"F0.wireOp",EDGE,"E21");Q42=makeQuery(id+"F1.opExtrude","CAP_EDGE",EDGE,{"disambiguationData":[OSD([subQ0]),TDD([makeQuery(id+"F0.imprint","IMPRINT",EDGE,{"disambiguationData":[TD([[makeQuery(id+"F0.imprint","INTERSECT",VERTEX,{"derivedFrom":[subQ0,sQuery(id+"F0.wireOp",EDGE,"E23")]}),1.0]])],"derivedFrom":subQ0})])],"isStart":true});}
            var Q43;
            Q43=makeQuery(id+"F1.opExtrude","CAP_EDGE",EDGE,{"disambiguationData":[OSD([sQuery(id+"F0.wireOp",EDGE,"E24")])],"isStart":true});
            fillet(context, id + "F2", {"entities" : qUnion([Q0, Q1, Q2, Q3, Q4, Q5, Q6, Q7, Q8, Q9, Q10, Q11, Q12, Q13, Q14, Q15, Q16, Q17, Q18, Q19, Q20, Q21, Q22, Q23, Q24, Q25, Q26, Q27, Q28, Q29, Q30, Q31, Q32, Q33, Q34, Q35, Q36, Q37, Q38, Q39, Q40, Q41, Q42, Q43]), "radius" : 0.64 * mm, "tangentPropagation" : true, "allowEdgeOverflow" : false});
        }
        {
            var Q0;
            Q0=sQuery(id+"F0.wireOp",VERTEX,"E3.start");
            var Q1;
            Q1=sQuery(id+"F0.wireOp",VERTEX,"E4.center");
            var Q2;
            Q2=sQuery(id+"F0.wireOp",VERTEX,"E34.center");
            var Q3;
            Q3=sQuery(id+"F0.wireOp",VERTEX,"E21.center");
            var Q4;
            Q4=makeQuery(id+"F1.opExtrude","SWEPT_BODY",BODY,{"disambiguationData":[OSD([sQuery(id+"F0.wireOp",EDGE,"E0"),sQuery(id+"F0.wireOp",EDGE,"E4"),sQuery(id+"F0.wireOp",EDGE,"E6"),sQuery(id+"F0.wireOp",EDGE,"E7"),sQuery(id+"F0.wireOp",EDGE,"E15"),sQuery(id+"F0.wireOp",EDGE,"E16"),sQuery(id+"F0.wireOp",EDGE,"E17"),sQuery(id+"F0.wireOp",EDGE,"E18"),sQuery(id+"F0.wireOp",EDGE,"E21"),sQuery(id+"F0.wireOp",EDGE,"E23"),sQuery(id+"F0.wireOp",EDGE,"E24"),sQuery(id+"F0.wireOp",EDGE,"E29"),sQuery(id+"F0.wireOp",EDGE,"E30"),sQuery(id+"F0.wireOp",EDGE,"E34"),sQuery(id+"F0.wireOp",EDGE,"E36"),sQuery(id+"F0.wireOp",EDGE,"E37"),sQuery(id+"F0.wireOp",EDGE,"E42"),sQuery(id+"F0.wireOp",EDGE,"E43"),sQuery(id+"F0.wireOp",EDGE,"E53"),sQuery(id+"F0.wireOp",EDGE,"E54"),sQuery(id+"F0.wireOp",EDGE,"E55"),sQuery(id+"F0.wireOp",EDGE,"E56")])]});
            hole(context, id + "F3", {"style" : HoleStyle.SIMPLE, "endStyle" : HoleEndStyle.THROUGH, "oppositeDirection" : true, "holeDiameter" : 22 * mm, "isTappedThrough" : true, "tappedDepth" : 12.7 * mm, "tapClearance" : 3, "locations" : qUnion([Q0, Q1, Q2, Q3]), "scope" : qUnion([Q4])});
        }
    });
